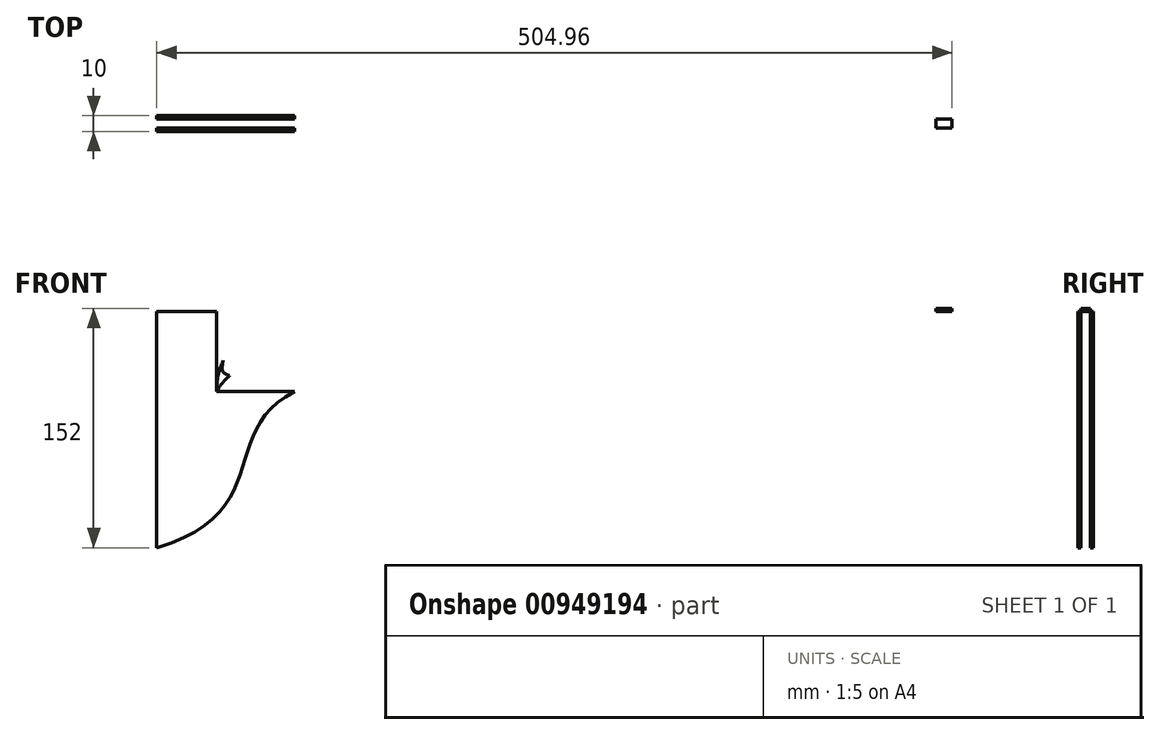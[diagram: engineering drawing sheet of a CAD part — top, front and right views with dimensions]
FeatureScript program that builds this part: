
annotation { "Feature Type Name" : "Feature", "Feature Type Description" : "" }
export const myFeature = defineFeature(function(context is Context, id is Id, definition is map)
    precondition{}
    {
        {
            var Q0;
            Q0=qCreatedBy(makeId("Front.planeOp"),FACE);
            var sketch = newSketch(context, id + "F0", { "sketchPlane" : qUnion([Q0])});
            skLineSegment(sketch, "E0.top", {"start": v(0, 150) * mm, "end": v(504.96, 150) * mm});
            skLineSegment(sketch, "E0.left", {"start": v(0, 0) * mm, "end": v(0, 150) * mm});
            skLineSegment(sketch, "E1", {"start": v(0, 0) * mm, "end": v(504.96, 150) * mm});
            skPoint(sketch, "E2", {"position": v(500, 150.62) * mm});
            skFitSpline(sketch, "E3", {"points": [v(0, 0) * mm, v(72.6, 88.48) * mm, v(504.96, 150) * mm], "startDerivative": vector(584.37, 173.59) * mm, "endDerivative": vector(688.49, 74.25) * mm});
            skLineSegment(sketch, "E4", {"start": v(37.9, 163.91) * mm, "end": v(37.9, 99.42) * mm});
            skLineSegment(sketch, "E5", {"start": v(37.9, 99.42) * mm, "end": v(37.9, 163.91) * mm});
            skLineSegment(sketch, "E6", {"start": v(185.03, 163.91) * mm, "end": v(37.9, 163.91) * mm});
            skLineSegment(sketch, "E7", {"start": v(37.9, 99.42) * mm, "end": v(254.8, 99.42) * mm});
            skPoint(sketch, "E8", {"position": v(84.35, 99.42) * mm});
            skPoint(sketch, "E9", {"position": v(84.35, 163.91) * mm});
            skArc(sketch, "E10", {"start": v(37.9, 99.42) * mm, "mid": v(51.5, 132.27) * mm, "end": v(84.35, 145.87) * mm});
            skLineSegment(sketch, "E11", {"start": v(84.35, 145.87) * mm, "end": v(376.77, 145.87) * mm});
            skPoint(sketch, "E12.1.internal.snap0", {"position": v(51.5, 132.27) * mm});
            skFitSpline(sketch, "E13", {"points": [v(37.9, 99.42) * mm, v(56.34, 115.22) * mm, v(376.77, 145.87) * mm], "startDerivative": vector(50.96, 77.27) * mm, "endDerivative": vector(535.08, 25.56) * mm});
            skFitSpline(sketch, "E14", {"points": [v(42.22, 118.97) * mm, v(42.54, 111.3) * mm, v(46.3, 109.38) * mm, v(46.3, 109.39) * mm], "startDerivative": vector(-4.23, -16.26) * mm, "endDerivative": vector(0.14, 0.45) * mm});
            skSolve(sketch);
        }
        {
            var Q0;
            Q0=makeQuery(id+"F0.imprint","IMPRINT",FACE,{"disambiguationData":[TD([[makeQuery(id+"F0.imprint","IMPRINT",EDGE,{"derivedFrom":sQuery(id+"F0.wireOp",EDGE,"E0.top")}),-1.0]])]});
            var Q1;
            {var subQ0=sQuery(id+"F0.wireOp",EDGE,"E0.left");Q1=makeQuery(id+"F0.imprint","IMPRINT",FACE,{"disambiguationData":[TD([[makeQuery(id+"F0.imprint","IMPRINT",EDGE,{"derivedFrom":subQ0}),-1.0]])]});}
            var Q2;
            {var subQ1=sQuery(id+"F0.wireOp",EDGE,"E10");Q2=makeQuery(id+"F0.imprint","IMPRINT",FACE,{"disambiguationData":[TD([[makeQuery(id+"F0.imprint","IMPRINT",EDGE,{"derivedFrom":subQ1}),1.0]])]});}
            var Q3;
            {var subQ1=sQuery(id+"F0.wireOp",EDGE,"E10");var subQ3=sQuery(id+"F0.wireOp",EDGE,"E14");var subQ4=makeQuery(id+"F0.imprint","INTERSECT",VERTEX,{"derivedFrom":[subQ1,subQ3]});Q3=makeQuery(id+"F0.imprint","IMPRINT",FACE,{"disambiguationData":[TD([[makeQuery(id+"F0.imprint","IMPRINT",EDGE,{"disambiguationData":[TD([[subQ4,-1.0]])],"derivedFrom":subQ3}),-1.0]])]});}
            var Q4;
            Q4=sQuery(id+"F0.wireOp",EDGE,"E0.top");
            var Q5;
            Q5=sQuery(id+"F0.wireOp",EDGE,"E0.left");
            var Q6;
            Q6=sQuery(id+"F0.wireOp",EDGE,"Jw0Kko6Y-Kxy0-Mjby-PuqF-n3pMdOWkgguy");
            var Q7;
            Q7=sQuery(id+"F0.wireOp",EDGE,"E3");
            extrude(context, id + "F1", {"entities" : qUnion([Q0, Q1, Q2, Q3]), "surfaceEntities" : qUnion([Q4, Q5, Q6, Q7]), "depth" : 10 * mm, "offsetDistance" : 25 * mm});
        }
        {
            var Q0;
            Q0=makeQuery(id+"F1.opExtrude","SWEPT_FACE",FACE,{"disambiguationData":[OSD([sQuery(id+"F0.wireOp",EDGE,"E0.top")])]});
            var sketch = newSketch(context, id + "F2", { "sketchPlane" : qUnion([Q0])});
            skLineSegment(sketch, "E15", {"start": v(0, -2) * mm, "end": v(504.96, -2) * mm});
            skLineSegment(sketch, "E16", {"start": v(504.96, -8) * mm, "end": v(0, -8) * mm});
            skLineSegment(sketch, "E17.bottom", {"start": v(504.96, 0) * mm, "end": v(494.96, 0) * mm});
            skLineSegment(sketch, "E17.top", {"start": v(504.96, -10) * mm, "end": v(494.96, -10) * mm});
            skLineSegment(sketch, "E17.left", {"start": v(504.96, 0) * mm, "end": v(504.96, -10) * mm});
            skLineSegment(sketch, "E17.right", {"start": v(494.96, 0) * mm, "end": v(494.96, -10) * mm});
            skSolve(sketch);
        }
        {
            var Q0;
            {var subQ0=sQuery(id+"F2.wireOp",EDGE,"E17.left");var subQ1=sQuery(id+"F2.wireOp",EDGE,"E15");var subQ2=makeQuery(id+"F2.imprint","INTERSECT",VERTEX,{"derivedFrom":[subQ1,subQ0]});Q0=makeQuery(id+"F2.imprint","IMPRINT",FACE,{"disambiguationData":[TD([[makeQuery(id+"F2.imprint","IMPRINT",EDGE,{"disambiguationData":[TD([[subQ2,1.0]])],"derivedFrom":subQ1}),-1.0]])]});}
            var Q1;
            {var subQ5=sQuery(id+"F2.wireOp",EDGE,"E17.bottom");Q1=makeQuery(id+"F2.imprint","IMPRINT",FACE,{"disambiguationData":[TD([[makeQuery(id+"F2.imprint","IMPRINT",EDGE,{"derivedFrom":subQ5}),-1.0]])]});}
            var Q2;
            {var subQ5=sQuery(id+"F2.wireOp",EDGE,"E17.top");Q2=makeQuery(id+"F2.imprint","IMPRINT",FACE,{"disambiguationData":[TD([[makeQuery(id+"F2.imprint","IMPRINT",EDGE,{"derivedFrom":subQ5}),1.0]])]});}
            extrude(context, id + "F3", {"entities" : qUnion([Q0, Q1, Q2]), "depth" : 2 * mm, "offsetDistance" : 25 * mm});
        }
        {
            var Q0;
            {var subQ0=sQuery(id+"F2.wireOp",EDGE,"E15");Q0=makeQuery(id+"F2.imprint","IMPRINT",FACE,{"disambiguationData":[TD([[makeQuery(id+"F2.imprint","IMPRINT",EDGE,{"derivedFrom":subQ0}),-1.0]])]});}
            extrude(context, id + "F4", {"entities" : qUnion([Q0]), "operationType" : NewBodyOperationType.REMOVE, "endBound" : BoundingType.THROUGH_ALL, "oppositeDirection" : true, "depth" : 25 * mm, "offsetDistance" : 25 * mm});
        }
    });
